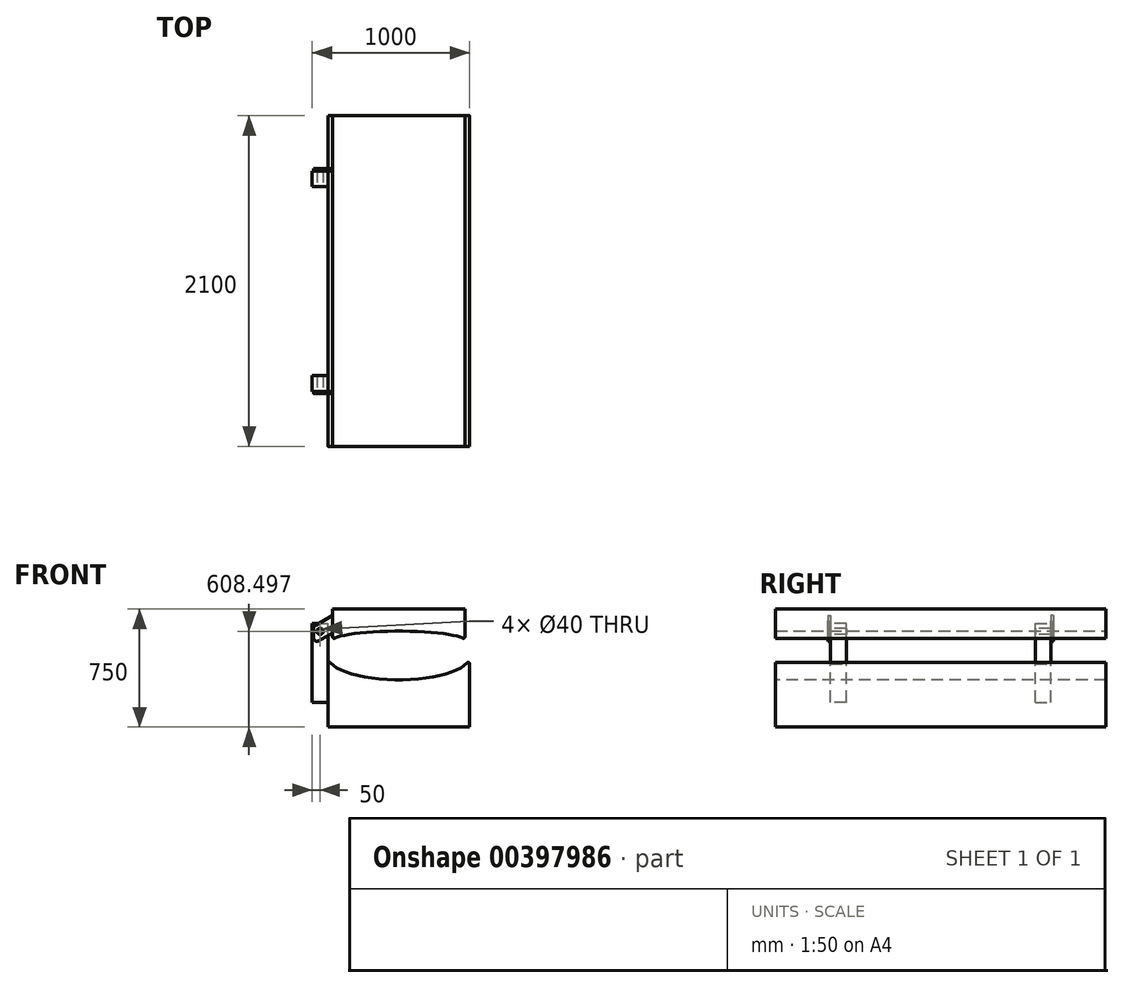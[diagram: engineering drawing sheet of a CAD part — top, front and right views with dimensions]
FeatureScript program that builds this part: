
annotation { "Feature Type Name" : "Feature", "Feature Type Description" : "" }
export const myFeature = defineFeature(function(context is Context, id is Id, definition is map)
    precondition{}
    {
        {
            var Q0;
            Q0=qCreatedBy(makeId("Front.planeOp"),FACE);
            var sketch = newSketch(context, id + "F0", { "sketchPlane" : qUnion([Q0])});
            skLineSegment(sketch, "E0", {"start": v(0, 0) * mm, "end": v(-450, 0) * mm});
            skLineSegment(sketch, "E1", {"start": v(-450, 0) * mm, "end": v(-450, 401.96) * mm});
            skLineSegment(sketch, "E2", {"start": v(0, 0) * mm, "end": v(0, 300) * mm, "construction": true});
            skEllipticalArc(sketch, "E3", {});
            skLineSegment(sketch, "E4.MirrorCS", {"start": v(0, 0) * mm, "end": v(450, 0) * mm});
            skLineSegment(sketch, "E5.MirrorCS", {"start": v(450, 0) * mm, "end": v(450, 401.96) * mm});
            skPoint(sketch, "E6.visualSharp", {"position": v(-450, 450) * mm});
            skArc(sketch, "E6.filletArc", {"start": v(-432.43, 408.5) * mm, "mid": v(-443.49, 411.33) * mm, "end": v(-450, 401.96) * mm});
            skPoint(sketch, "E7.visualSharp", {"position": v(450, 450) * mm});
            skArc(sketch, "E7.filletArc", {"start": v(450, 401.96) * mm, "mid": v(443.49, 411.33) * mm, "end": v(432.43, 408.5) * mm});
            const initialGuessF0  = {"E3": [0, 0.45, 0, -1, 0.15, 0.45, 4.992731755272947, 1.2904535524301268]};
            skSetInitialGuess(sketch, initialGuessF0);
            skSolve(sketch);
        }
        {
            var Q0;
            Q0=makeQuery(id+"F0.imprint","IMPRINT",FACE,{"disambiguationData":[TD([[makeQuery(id+"F0.imprint","IMPRINT",EDGE,{"derivedFrom":sQuery(id+"F0.wireOp",EDGE,"E0")}),-1.0]])]});
            extrude(context, id + "F1", {"entities" : qUnion([Q0]), "depth" : 1050 * mm, "offsetDistance" : 25 * mm, "hasSecondDirection" : true, "secondDirectionOppositeDirection" : true, "secondDirectionDepth" : 1050 * mm});
        }
        {
            var Q0;
            Q0=makeQuery(id+"F1.opExtrude","SWEPT_FACE",FACE,{"disambiguationData":[OSD([sQuery(id+"F0.wireOp",EDGE,"E1")])]});
            var sketch = newSketch(context, id + "F2", { "sketchPlane" : qUnion([Q0])});
            skLineSegment(sketch, "E8.bottom", {"start": v(600, 158.5) * mm, "end": v(700, 158.5) * mm});
            skLineSegment(sketch, "E8.top", {"start": v(600, 658.5) * mm, "end": v(700, 658.5) * mm});
            skLineSegment(sketch, "E8.left", {"start": v(600, 158.5) * mm, "end": v(600, 658.5) * mm});
            skLineSegment(sketch, "E8.right", {"start": v(700, 158.5) * mm, "end": v(700, 658.5) * mm});
            skLineSegment(sketch, "E9", {"start": v(0, 0) * mm, "end": v(0, 831.53) * mm, "construction": true});
            skPoint(sketch, "E9.endSnap0", {"position": v(0, 0) * mm});
            skLineSegment(sketch, "E10.MirrorCS", {"start": v(-600, 158.5) * mm, "end": v(-700, 158.5) * mm});
            skLineSegment(sketch, "E11.MirrorCS", {"start": v(-600, 658.5) * mm, "end": v(-700, 658.5) * mm});
            skLineSegment(sketch, "E12.MirrorCS", {"start": v(-700, 158.5) * mm, "end": v(-700, 658.5) * mm});
            skLineSegment(sketch, "E13.MirrorCS", {"start": v(-600, 158.5) * mm, "end": v(-600, 658.5) * mm});
            skSolve(sketch);
        }
        {
            var Q0;
            {var subQ0=sQuery(id+"F2.wireOp",EDGE,"E11.MirrorCS");Q0=makeQuery(id+"F2.imprint","IMPRINT",FACE,{"disambiguationData":[TD([[makeQuery(id+"F2.imprint","IMPRINT",EDGE,{"derivedFrom":subQ0}),1.0]])]});}
            var Q1;
            {var subQ0=sQuery(id+"F2.wireOp",EDGE,"E10.MirrorCS");Q1=makeQuery(id+"F2.imprint","IMPRINT",FACE,{"disambiguationData":[TD([[makeQuery(id+"F2.imprint","IMPRINT",EDGE,{"derivedFrom":subQ0}),-1.0]])]});}
            var Q2;
            {var subQ0=sQuery(id+"F2.wireOp",EDGE,"E8.bottom");Q2=makeQuery(id+"F2.imprint","IMPRINT",FACE,{"disambiguationData":[TD([[makeQuery(id+"F2.imprint","IMPRINT",EDGE,{"derivedFrom":subQ0}),1.0]])]});}
            var Q3;
            {var subQ0=sQuery(id+"F2.wireOp",EDGE,"E8.top");Q3=makeQuery(id+"F2.imprint","IMPRINT",FACE,{"disambiguationData":[TD([[makeQuery(id+"F2.imprint","IMPRINT",EDGE,{"derivedFrom":subQ0}),-1.0]])]});}
            extrude(context, id + "F3", {"entities" : qUnion([Q0, Q1, Q2, Q3]), "operationType" : NewBodyOperationType.ADD, "depth" : 100 * mm, "offsetDistance" : 25 * mm});
        }
        {
            var Q0;
            Q0=makeQuery(id+"F3.opExtrude","SWEPT_FACE",FACE,{"disambiguationData":[OSD([sQuery(id+"F2.wireOp",EDGE,"E8.right")])]});
            var sketch = newSketch(context, id + "F4", { "sketchPlane" : qUnion([Q0])});
            skCircle(sketch, "E14", {"center": v(-500, 608.5) * mm, "radius": 20 * mm});
            skSolve(sketch);
        }
        {
            var Q0;
            Q0=makeQuery(id+"F4.imprint","IMPRINT",FACE,{"disambiguationData":[TD([[makeQuery(id+"F4.imprint","IMPRINT",EDGE,{"derivedFrom":sQuery(id+"F4.wireOp",EDGE,"E14")}),1.0]])]});
            var Q1;
            Q1=makeQuery(id+"F3.opExtrude","SWEPT_FACE",FACE,{"disambiguationData":[OSD([sQuery(id+"F2.wireOp",EDGE,"E12.MirrorCS")])]});
            extrude(context, id + "F5", {"entities" : qUnion([Q0]), "operationType" : NewBodyOperationType.REMOVE, "endBound" : BoundingType.UP_TO_SURFACE, "oppositeDirection" : true, "depth" : 25 * mm, "endBoundEntityFace" : qUnion([Q1]), "offsetDistance" : 25 * mm});
        }
        {
            var Q0;
            Q0=qCreatedBy(makeId("Front.planeOp"),FACE);
            var sketch = newSketch(context, id + "F6", { "sketchPlane" : qUnion([Q0])});
            skLineSegment(sketch, "E15", {"start": v(0, 447.23) * mm, "end": v(0, 750) * mm, "construction": true});
            skLineSegment(sketch, "E16", {"start": v(0, 750) * mm, "end": v(-420, 750) * mm});
            skLineSegment(sketch, "E17", {"start": v(-420, 750) * mm, "end": v(-420, 574.56) * mm});
            skEllipticalArc(sketch, "E18", {});
            skLineSegment(sketch, "E19.MirrorCS", {"start": v(0, 750) * mm, "end": v(420, 750) * mm});
            skLineSegment(sketch, "E20.MirrorCS", {"start": v(420, 750) * mm, "end": v(420, 574.56) * mm});
            skPoint(sketch, "E21.visualSharp", {"position": v(-420, 550) * mm});
            skArc(sketch, "E21.filletArc", {"start": v(-420, 574.56) * mm, "mid": v(-415.17, 566) * mm, "end": v(-405.34, 565.71) * mm});
            skPoint(sketch, "E22.visualSharp", {"position": v(420, 550) * mm});
            skArc(sketch, "E22.filletArc", {"start": v(405.34, 565.71) * mm, "mid": v(415.17, 566) * mm, "end": v(420, 574.56) * mm});
            const initialGuessF6  = {"E18": [0, 0.55, 1, 0, 0.42, 0.06, 0.264975351904304, 2.8766173016854903]};
            skSetInitialGuess(sketch, initialGuessF6);
            skSolve(sketch);
        }
        {
            var Q0;
            Q0=makeQuery(id+"F6.imprint","IMPRINT",FACE,{"disambiguationData":[TD([[makeQuery(id+"F6.imprint","IMPRINT",EDGE,{"derivedFrom":sQuery(id+"F6.wireOp",EDGE,"E16")}),1.0]])]});
            var Q1;
            Q1=makeQuery(id+"F1.opExtrude","CAP_FACE",FACE,{"disambiguationData":[OSD([sQuery(id+"F0.wireOp",EDGE,"E0"),sQuery(id+"F0.wireOp",EDGE,"E1"),sQuery(id+"F0.wireOp",EDGE,"E3"),sQuery(id+"F0.wireOp",EDGE,"E4.MirrorCS"),sQuery(id+"F0.wireOp",EDGE,"E5.MirrorCS"),sQuery(id+"F0.wireOp",EDGE,"E6.filletArc"),sQuery(id+"F0.wireOp",EDGE,"E7.filletArc")])],"isStart":false});
            var Q2;
            Q2=makeQuery(id+"F1.opExtrude","SWEPT_BODY",BODY,{"disambiguationData":[OSD([sQuery(id+"F0.wireOp",EDGE,"E0"),sQuery(id+"F0.wireOp",EDGE,"E1"),sQuery(id+"F0.wireOp",EDGE,"E3"),sQuery(id+"F0.wireOp",EDGE,"E4.MirrorCS"),sQuery(id+"F0.wireOp",EDGE,"E5.MirrorCS"),sQuery(id+"F0.wireOp",EDGE,"E6.filletArc"),sQuery(id+"F0.wireOp",EDGE,"E7.filletArc")])]});
            var Q3;
            Q3=makeQuery(id+"F1.opExtrude","CAP_FACE",FACE,{"disambiguationData":[OSD([sQuery(id+"F0.wireOp",EDGE,"E0"),sQuery(id+"F0.wireOp",EDGE,"E1"),sQuery(id+"F0.wireOp",EDGE,"E3"),sQuery(id+"F0.wireOp",EDGE,"E4.MirrorCS"),sQuery(id+"F0.wireOp",EDGE,"E5.MirrorCS"),sQuery(id+"F0.wireOp",EDGE,"E6.filletArc"),sQuery(id+"F0.wireOp",EDGE,"E7.filletArc")])],"isStart":true});
            extrude(context, id + "F7", {"entities" : qUnion([Q0]), "endBound" : BoundingType.UP_TO_SURFACE, "depth" : 950 * mm, "endBoundEntityFace" : qUnion([Q1]), "endBoundEntityBody" : qUnion([Q2]), "offsetDistance" : 25 * mm, "hasSecondDirection" : true, "secondDirectionBound" : SecondDirectionBoundingType.UP_TO_SURFACE, "secondDirectionOppositeDirection" : true, "secondDirectionDepth" : 26 * mm, "secondDirectionBoundEntityFace" : qUnion([Q3])});
        }
        {
            var Q0;
            Q0=makeQuery(id+"F3.opExtrude","SWEPT_FACE",FACE,{"disambiguationData":[OSD([sQuery(id+"F2.wireOp",EDGE,"E8.right")])]});
            var sketch = newSketch(context, id + "F8", { "sketchPlane" : qUnion([Q0])});
            skLineSegment(sketch, "E23", {"start": v(-420, 710) * mm, "end": v(-530, 646.5) * mm});
            skLineSegment(sketch, "E24", {"start": v(-540, 629.17) * mm, "end": v(-540, 565.36) * mm});
            skLineSegment(sketch, "E25", {"start": v(-510, 548.04) * mm, "end": v(-420, 600) * mm});
            skLineSegment(sketch, "E26", {"start": v(-420, 600) * mm, "end": v(-420, 710) * mm});
            skPoint(sketch, "E27.visualSharp", {"position": v(-540, 640.72) * mm});
            skArc(sketch, "E27.filletArc", {"start": v(-530, 646.5) * mm, "mid": v(-537.32, 639.17) * mm, "end": v(-540, 629.17) * mm});
            skPoint(sketch, "E28.visualSharp", {"position": v(-540, 530.72) * mm});
            skArc(sketch, "E28.filletArc", {"start": v(-540, 565.36) * mm, "mid": v(-530, 548.04) * mm, "end": v(-510, 548.04) * mm});
            skSolve(sketch);
        }
        {
            var Q0;
            {var subQ7=sQuery(id+"F8.wireOp",EDGE,"E26");Q0=makeQuery(id+"F8.imprint","IMPRINT",FACE,{"disambiguationData":[TD([[makeQuery(id+"F8.imprint","IMPRINT",EDGE,{"derivedFrom":subQ7}),1.0]])]});}
            var Q1;
            Q1=makeQuery(id+"F8.imprint","IMPRINT",FACE,{"disambiguationData":[TD([[makeQuery(id+"F8.imprint","IMPRINT",EDGE,{"derivedFrom":sQuery(id+"F8.wireOp",EDGE,"E24")}),1.0]])]});
            extrude(context, id + "F9", {"entities" : qUnion([Q0, Q1]), "depth" : 15 * mm, "offsetDistance" : 25 * mm});
        }
        {
            var Q0;
            Q0=makeQuery(id+"F9.opExtrude","SWEPT_BODY",BODY,{"disambiguationData":[OSD([sQuery(id+"F4.wireOp",EDGE,"E14"),sQuery(id+"F8.wireOp",EDGE,"E23"),sQuery(id+"F8.wireOp",EDGE,"E24"),sQuery(id+"F8.wireOp",EDGE,"E25"),sQuery(id+"F8.wireOp",EDGE,"E26"),sQuery(id+"F8.wireOp",EDGE,"E27.filletArc"),sQuery(id+"F8.wireOp",EDGE,"E28.filletArc")])]});
            var Q1;
            Q1=qCreatedBy(makeId("Front.planeOp"),FACE);
            mirror(context, id + "F10", {"entities" : qUnion([Q0]), "mirrorPlane" : qUnion([Q1])});
        }
    });
